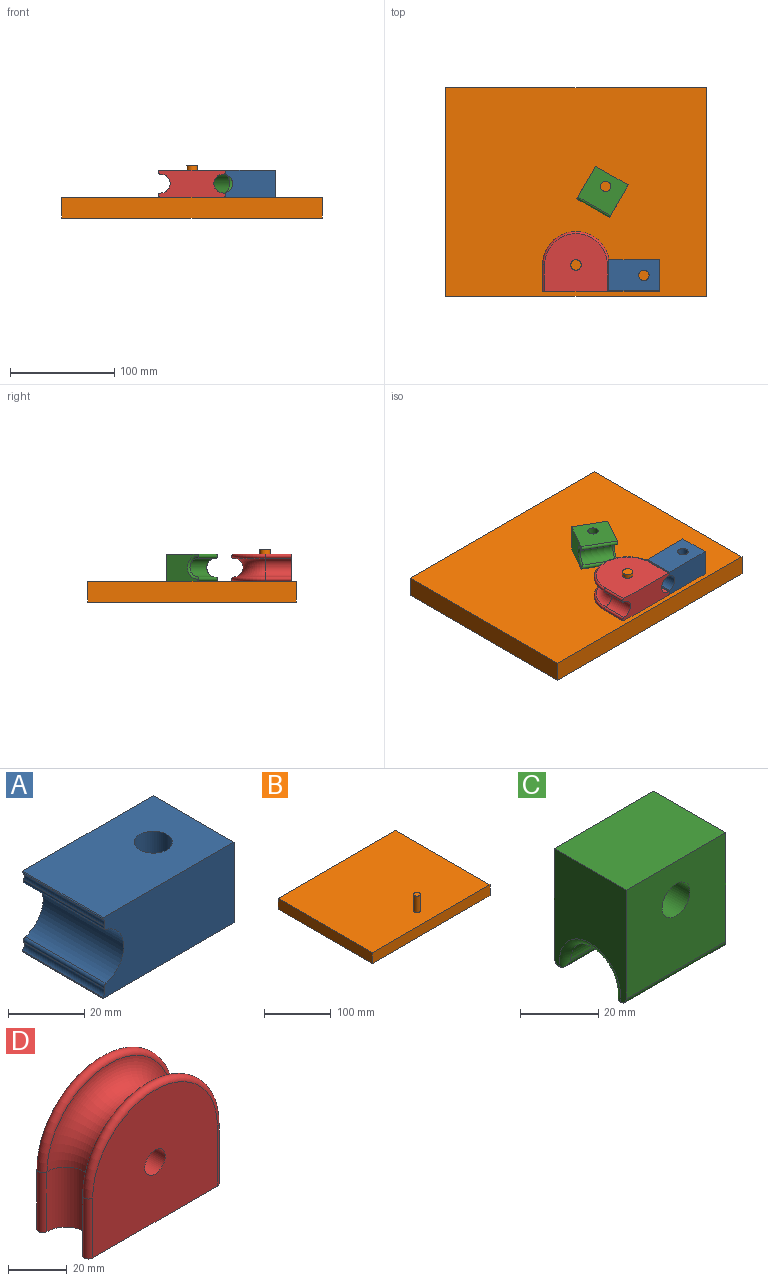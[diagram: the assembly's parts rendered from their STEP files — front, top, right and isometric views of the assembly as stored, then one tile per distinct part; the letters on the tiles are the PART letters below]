
ASSEMBLY  parts=4 mates=4
PART A: 13 faces, bbox 48.8x30x26 mm
  f0: plane 48.84x26mm, normal (0,-1,0), area 1158.6mm2, adj f1,f4,f5,f6,f7,f8,f9,f10
  f1: plane 30x26mm, normal (1,0,0), area 780mm2, adj f0,f2,f4,f5
  f2: plane 48.84x26mm, normal (0,1,0), area 1158.6mm2, adj f1,f4,f5,f6,f7,f8,f9,f10
  f3: cylinder r=5mm len=26mm, axis (0,0,-1), area 816.8mm2, adj f4,f5
  f4: plane 48.59x30mm, normal (0,0,1), area 1379mm2, adj f0,f1,f2,f3,f12
  f5: plane 48.59x30mm, normal (0,0,-1), area 1379mm2, adj f0,f1,f2,f3,f11
  f6: cylinder r=9mm len=30mm, axis (0,-1,0), area 702.2mm2, adj f0,f2,f9,f10
  f7: cylinder r=2mm len=30mm, axis (0,-1,0), area 81.8mm2, adj f0,f2,f9,f11
  f8: cylinder r=2mm len=30mm, axis (0,-1,0), area 81.8mm2, adj f0,f2,f10,f12
  f9: cylinder r=1mm len=30mm, axis (0,-1,0), area 53.2mm2, adj f0,f2,f6,f7
  f10: cylinder r=1mm len=30mm, axis (0,-1,0), area 53.2mm2, adj f0,f2,f6,f8
  f11: cylinder r=0.25mm len=30mm, axis (0,-1,0), area 18.5mm2, adj f0,f2,f5,f7
  f12: cylinder r=0.25mm len=30mm, axis (0,-1,0), area 18.5mm2, adj f0,f2,f4,f8
PART B: 8 faces, bbox 250x200x50 mm
  f0: plane 200x20mm, normal (-1,0,0), area 4000mm2, adj f1,f3,f4,f5
  f1: plane 250x20mm, normal (0,-1,0), area 5000mm2, adj f0,f2,f4,f5
  f2: plane 200x20mm, normal (1,0,0), area 4000mm2, adj f1,f3,f4,f5
  f3: plane 250x20mm, normal (0,1,0), area 5000mm2, adj f0,f2,f4,f5
  f4: plane 250x200mm, normal (0,0,-1), area 50000mm2, adj f0,f1,f2,f3
  f5: plane 250x200mm, normal (0,0,1), area 49921.5mm2, adj f0,f1,f2,f3,f6
  f6: cylinder r=5mm len=30mm, axis (0,0,-1), area 942.5mm2, adj f5,f7
  f7: plane 10x10mm, normal (0,0,1), area 78.5mm2, adj f6
PART C: 11 faces, bbox 36x26.9x36.4 mm
  f0: plane 36x34mm, normal (0,-1,0), area 1145.5mm2, adj f2,f3,f4,f6,f8
  f1: plane 36x34mm, normal (0,1,0), area 1145.5mm2, adj f2,f3,f4,f7,f8
  f2: plane 36x26mm, normal (-1,0,0), area 700.5mm2, adj f0,f1,f4,f6,f7,f9
  f3: plane 36x26mm, normal (1,0,0), area 700.5mm2, adj f0,f1,f4,f6,f7,f10
  f4: plane 36x26mm, normal (0,0,1), area 936mm2, adj f0,f1,f2,f3
  f5: cylinder r=9mm len=32mm, axis (1,0,0), area 904.8mm2, adj f6,f7,f9,f10
  f6: cylinder r=2mm len=36mm, axis (1,0,0), area 222mm2, adj f0,f2,f3,f5,f9,f10
  f7: cylinder r=2mm len=36mm, axis (1,0,0), area 222mm2, adj f1,f2,f3,f5,f9,f10
  f8: cylinder r=5mm len=26mm, axis (0,-1,0), area 816.8mm2, adj f0,f1
  f9: torus R=11mm, axis (-1,0,0), area 103.6mm2, adj f2,f5,f6,f7
  f10: torus R=11mm, axis (-1,0,0), area 103.6mm2, adj f3,f5,f6,f7
PART D: 13 faces, bbox 78.8x26x64.4 mm
  f0: torus R=30mm, axis (0,-1,0), area 2155.9mm2, adj f1,f4,f5,f8
  f1: torus R=30mm, axis (0,-1,0), area 617.3mm2, adj f0,f2,f6,f7
  f2: plane 60x55mm, normal (0,-1,0), area 2835.2mm2, adj f1,f6,f7,f11,f12
  f3: plane 60x55mm, normal (0,1,0), area 2835.2mm2, adj f4,f9,f10,f11,f12
  f4: torus R=30mm, axis (0,-1,0), area 617.3mm2, adj f0,f3,f9,f10
  f5: cylinder r=9mm len=25mm, axis (0,0,1), area 706.9mm2, adj f0,f6,f10,f11
  f6: cylinder r=2mm len=25mm, axis (0,0,1), area 157.1mm2, adj f1,f2,f5,f11
  f7: cylinder r=2mm len=25mm, axis (0,0,1), area 157.1mm2, adj f1,f2,f8,f11
  f8: cylinder r=9mm len=25mm, axis (0,0,1), area 706.9mm2, adj f0,f7,f9,f11
  f9: cylinder r=2mm len=25mm, axis (0,0,1), area 157.1mm2, adj f3,f4,f8,f11
  f10: cylinder r=2mm len=25mm, axis (0,0,1), area 157.1mm2, adj f3,f4,f5,f11
  f11: plane 64x26mm, normal (0,0,-1), area 1330.7mm2, adj f2,f3,f5,f6,f7,f8,f9,f10
  f12: cylinder r=5mm len=26mm, axis (0,-1,0), area 816.8mm2, adj f2,f3
PLACE A t=(155.25,4.87,20.25)mm
PLACE B t=(0.23,-0.2,20.25)mm fixed
PLACE C rot(axis=(-0.94,0.25,-0.25),93.8deg) t=(157.33,75.28,20.25)mm
PLACE D rot(axis=(-1,0,0),90deg) t=(125.23,29.8,33.25)mm
MATE planar C.f1 <-> B.f5  axis (0,0,-1) through (150.99,100.42,20.25)mm
MATE slider B.f6 <-> D.f0  axis (0,0,-1) through (125.23,29.8,35.25)mm
MATE planar D.f3 <-> B.f5  axis (0,0,-1) through (125.23,29.54,20.25)mm
MATE planar A.f5 <-> B.f5  axis (0,0,-1) through (180.43,19.87,20.25)mm
